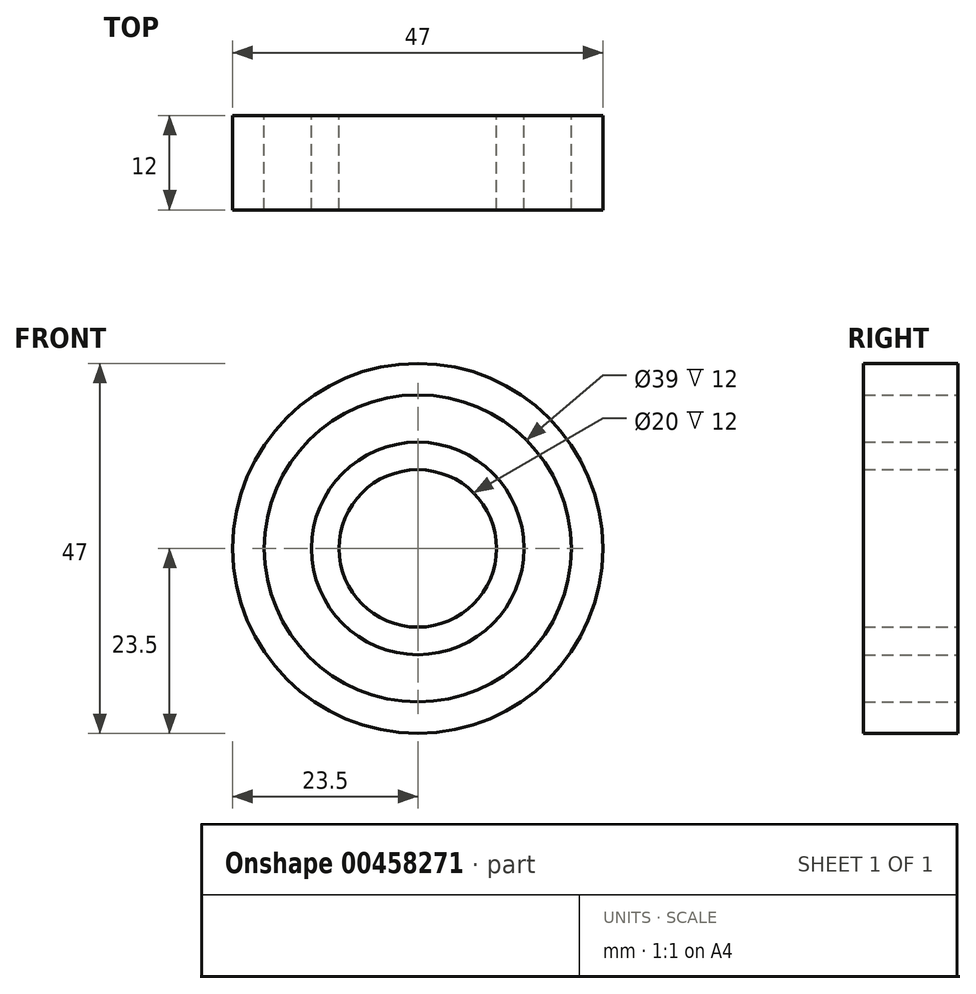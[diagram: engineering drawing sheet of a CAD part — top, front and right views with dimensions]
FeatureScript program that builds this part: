
annotation { "Feature Type Name" : "Feature", "Feature Type Description" : "" }
export const myFeature = defineFeature(function(context is Context, id is Id, definition is map)
    precondition{}
    {
        {
            var Q0;
            Q0=qCreatedBy(makeId("Front.planeOp"),FACE);
            var sketch = newSketch(context, id + "F0", { "sketchPlane" : qUnion([Q0])});
            skCircle(sketch, "E0", {"center": v(0, 0) * mm, "radius": 10 * mm});
            skCircle(sketch, "E1", {"center": v(0, 0) * mm, "radius": 13.5 * mm});
            skSolve(sketch);
        }
        {
            var Q0;
            Q0=makeQuery(id+"F0.imprint","IMPRINT",FACE,{"disambiguationData":[TD([[makeQuery(id+"F0.imprint","IMPRINT",EDGE,{"derivedFrom":sQuery(id+"F0.wireOp",EDGE,"E0")}),-1.0]])]});
            extrude(context, id + "F1", {"entities" : qUnion([Q0]), "depth" : 12 * mm});
        }
        {
            var Q0;
            Q0=qCreatedBy(makeId("Front.planeOp"),FACE);
            var sketch = newSketch(context, id + "F2", { "sketchPlane" : qUnion([Q0])});
            skCircle(sketch, "E2", {"center": v(0, 0) * mm, "radius": 19.5 * mm});
            skCircle(sketch, "E3", {"center": v(0, 0) * mm, "radius": 23.5 * mm});
            skSolve(sketch);
        }
        {
            var Q0;
            Q0=makeQuery(id+"F2.imprint","IMPRINT",FACE,{"disambiguationData":[TD([[makeQuery(id+"F2.imprint","IMPRINT",EDGE,{"derivedFrom":sQuery(id+"F2.wireOp",EDGE,"E2")}),-1.0]])]});
            var Q1;
            Q1=sQuery(id+"F2.wireOp",EDGE,"E3");
            extrude(context, id + "F3", {"entities" : qUnion([Q0]), "operationType" : NewBodyOperationType.ADD, "surfaceEntities" : qUnion([Q1]), "depth" : 12 * mm});
        }
        {
            var Q0;
            Q0=qCreatedBy(makeId("Front.planeOp"),FACE);
            cPlane(context, id + "F4", {"entities" : qUnion([Q0]), "cplaneType" : CPlaneType.OFFSET, "offset" : 6 * mm, "width" : 150 * mm, "height" : 150 * mm});
        }
        {
            var Q0;
            Q0=qCreatedBy(id+"F4.planeOp",FACE);
            var sketch = newSketch(context, id + "F5", { "sketchPlane" : qUnion([Q0])});
            skArc(sketch, "E4", {"start": v(0, 12.5) * mm, "mid": v(4, 16.5) * mm, "end": v(0, 20.5) * mm});
            skLineSegment(sketch, "E5", {"start": v(0, 12.5) * mm, "end": v(0, 20.5) * mm, "construction": true});
            skLineSegment(sketch, "E6", {"start": v(0, 12.5) * mm, "end": v(0, 20.5) * mm});
            skArc(sketch, "E7.1.0", {"start": v(-7.35, 10.11) * mm, "mid": v(-6.46, 15.7) * mm, "end": v(-12.05, 16.58) * mm});
            skArc(sketch, "E7.2.0", {"start": v(-11.89, 3.86) * mm, "mid": v(-14.46, 8.9) * mm, "end": v(-19.5, 6.33) * mm});
            skArc(sketch, "E7.3.0", {"start": v(-11.89, -3.86) * mm, "mid": v(-16.93, -1.3) * mm, "end": v(-19.5, -6.33) * mm});
            skArc(sketch, "E7.4.0", {"start": v(-7.35, -10.11) * mm, "mid": v(-12.93, -11) * mm, "end": v(-12.05, -16.58) * mm});
            skArc(sketch, "E7.5.0", {"start": v(0, -12.5) * mm, "mid": v(-4, -16.5) * mm, "end": v(0, -20.5) * mm});
            skArc(sketch, "E7.6.0", {"start": v(7.35, -10.11) * mm, "mid": v(6.46, -15.7) * mm, "end": v(12.05, -16.58) * mm});
            skArc(sketch, "E7.7.0", {"start": v(11.89, -3.86) * mm, "mid": v(14.46, -8.9) * mm, "end": v(19.5, -6.33) * mm});
            skArc(sketch, "E7.8.0", {"start": v(11.89, 3.86) * mm, "mid": v(16.93, 1.3) * mm, "end": v(19.5, 6.33) * mm});
            skArc(sketch, "E7.9.0", {"start": v(7.35, 10.11) * mm, "mid": v(12.93, 11) * mm, "end": v(12.05, 16.58) * mm});
            skPoint(sketch, "E7.center", {"position": v(0, 0) * mm});
            skSolve(sketch);
        }
        {
            var Q0;
            Q0=sQuery(id+"F5.wireOp",EDGE,"E4");
            var Q1;
            Q1=sQuery(id+"F5.wireOp",EDGE,"E6");
            revolve(context, id + "F6", {"bodyType" : ToolBodyType.SURFACE, "surfaceEntities" : qUnion([Q0]), "axis" : qUnion([Q1]), "revolveType" : RevolveType.FULL});
        }
        {
            var Q0;
            Q0=qCreatedBy(makeId("Right.planeOp"),FACE);
            var sketch = newSketch(context, id + "F7", { "sketchPlane" : qUnion([Q0])});
            skLineSegment(sketch, "E8", {"start": v(0, 0) * mm, "end": v(-39.98, 0) * mm, "construction": true});
            skSolve(sketch);
        }
        {
            var Q0;
            Q0=makeQuery(id+"F6.opRevolve","SWEPT_BODY",BODY,{"disambiguationData":[OSD([sQuery(id+"F5.wireOp",EDGE,"E4")])]});
            var Q1;
            Q1=sQuery(id+"F7.wireOp",EDGE,"E8");
            circularPattern(context, id + "F8", {"entities" : qUnion([Q0]), "axis" : qUnion([Q1]), "angle" : 360 * degree, "instanceCount" : 10, "equalSpace" : true});
        }
    });
